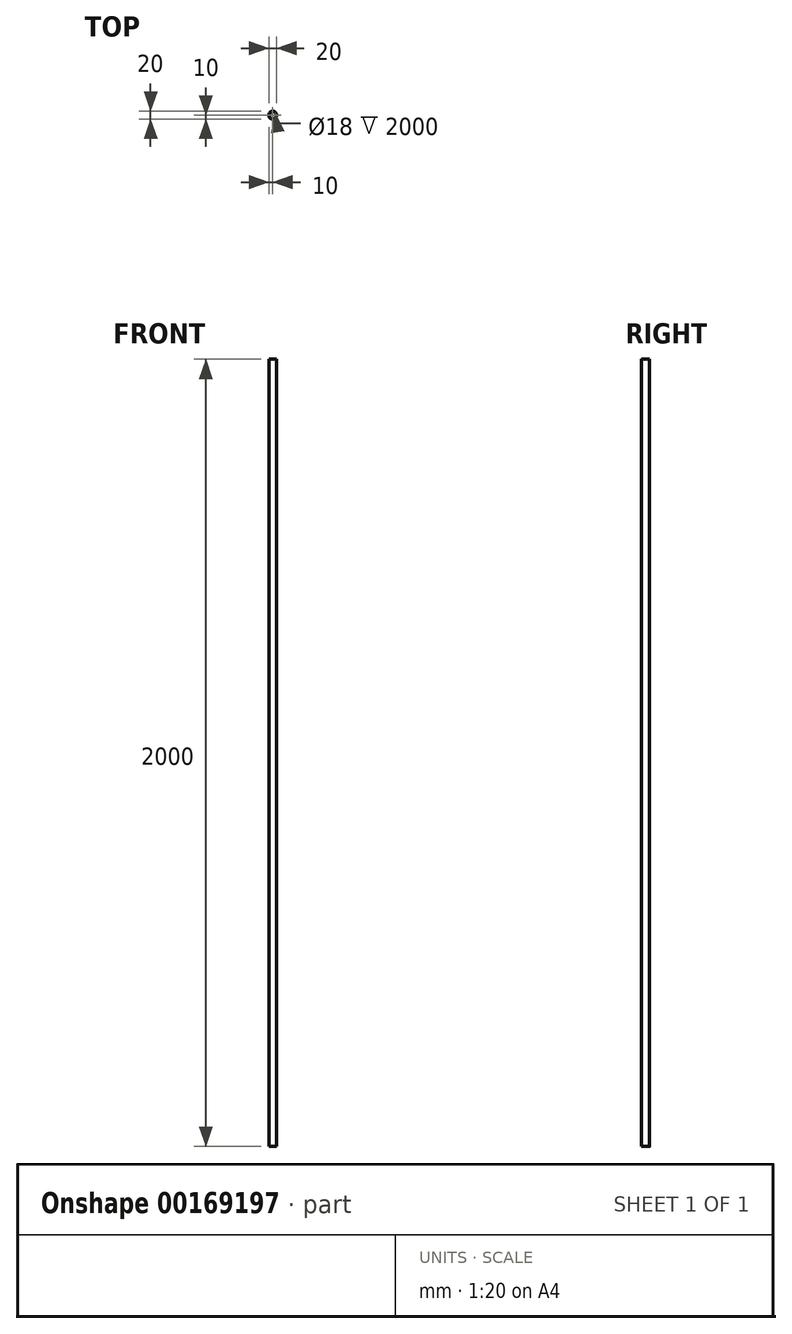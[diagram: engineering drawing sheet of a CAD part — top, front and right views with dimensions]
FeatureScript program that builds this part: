
annotation { "Feature Type Name" : "Feature", "Feature Type Description" : "" }
export const myFeature = defineFeature(function(context is Context, id is Id, definition is map)
    precondition{}
    {
        {
            var Q0;
            Q0=qCreatedBy(makeId("Top.planeOp"),FACE);
            var sketch = newSketch(context, id + "F0", { "sketchPlane" : qUnion([Q0])});
            skCircle(sketch, "E0", {"center": v(0, 0) * mm, "radius": 10 * mm});
            skSolve(sketch);
        }
        {
            var Q0;
            Q0=qCreatedBy(makeId("Top.planeOp"),FACE);
            var sketch = newSketch(context, id + "F1", { "sketchPlane" : qUnion([Q0])});
            skCircle(sketch, "E1", {"center": v(0, 0) * mm, "radius": 9 * mm});
            skSolve(sketch);
        }
        {
            var Q0;
            Q0 = qSketchRegion(id + "F0", true);
            extrude(context, id + "F2", {"entities" : qUnion([Q0]), "endBound" : BoundingType.SYMMETRIC, "oppositeDirection" : true, "depth" : 2000 * mm});
        }
        {
            var Q0;
            Q0 = qSketchRegion(id + "F1", true);
            extrude(context, id + "F3", {"entities" : qUnion([Q0]), "operationType" : NewBodyOperationType.REMOVE, "endBound" : BoundingType.THROUGH_ALL, "oppositeDirection" : true, "depth" : 25 * mm});
        }
        {
            var Q0;
            Q0 = qSketchRegion(id + "F1", true);
            extrude(context, id + "F4", {"entities" : qUnion([Q0]), "operationType" : NewBodyOperationType.REMOVE, "endBound" : BoundingType.THROUGH_ALL, "depth" : 25 * mm});
        }
    });
